# Revit family: SmartVide_120P_GENERADO
name_source: partatom
category: Equipos especializados
units: mm (PartAtom-declared; Revit-internal decimal feet)

## family parameters
Compartido = No
Corte con vacíos al cargar = No
Cota de conector redondo = Diámetro de uso
Número OmniClass = 23.21.21.13
Punto de cálculo de habitación = No
Se basa en plano de trabajo = No
Siempre vertical = Sí
Tipo de pieza = Normal

## types (8) — shared parameters
Fabricante = SAMMIC S.L.
Foodservice Equipment Identifier = Sí
Phase = 1
Revision Code = 1
URL = https://www.sammic.com
URL Cutsheet = http://www.sammic.com
zero-valued in all types: Elevación por defecto

## per-type parameters (varying)
| type | Comentarios de tipo | Conn Plug | Cycle | Depth | FL Amps | HP | Height | Modelo | Specification by Manufacturer | Volts | Watts | Weight in Pounds | Width |
| Heated tank 28P 28 l / 7.4 gal 230/50-60/1 | Tanks of 28 l / 7.4 gal and 56 l / 14.8 gal . | EU (SCHUKO 2P+G) | 50 Hz | 540 mm  [stored 1.77165 ft] | 3 A | 1.01 | 288 mm  [stored 0.944882 ft] | 1180070 | Connected to and controlled by SmartVide X to reach the set temperature faster. | 230 V | 750 W | 20.4 | 335 mm  [stored 1.09908 ft] |
| Heated tank 28P 28 l / 7.4 gal 120/60/1 | Tanks of 28 l / 7.4 gal and 56 l / 14.8 gal . | USA (NEMA 5-15P / 2P+G) | 60 Hz | 540 mm  [stored 1.77165 ft] | 6 A | 1.01 | 288 mm  [stored 0.944882 ft] | 1180071 | Connected to and controlled by SmartVide X to reach the set temperature faster. | 120 V | 750 W | 20.4 | 335 mm  [stored 1.09908 ft] |
| Heated tank 56P 56 l / 14.8 gal 230/50-60/1 | Tanks of 28 l / 7.4 gal and 56 l / 14.8 gal . | EU (SCHUKO 2P+G) | 50 Hz | 540 mm  [stored 1.77165 ft] | 6 A | 2.01 | 288 mm  [stored 0.944882 ft] | 1180075 | Connected to and controlled by SmartVide X to reach the set temperature faster. | 230 V | 1500 W | 36.8 | 660 mm  [stored 2.16535 ft] |
| Heated tank 56P 56 l / 14.8 gal 120/60/1 | Tanks of 28 l / 7.4 gal and 56 l / 14.8 gal . | USA (NEMA 5-15P / 2P+G) | 60 Hz | 540 mm  [stored 1.77165 ft] | 13 A | 2.01 | 288 mm  [stored 0.944882 ft] | 1180076 | Connected to and controlled by SmartVide X to reach the set temperature faster. | 120 V | 1500 W | 36.8 | 660 mm  [stored 2.16535 ft] |
| Heated tank 120 l / 30 gal SmartVide 120/60/1 | Connected to and controlled by SmartVide XL. | USA (NEMA 5-15P / 2P+G) | 60 Hz | 582 mm  [stored 1.90945 ft] | 13 A | 2.01 | 850 mm  [stored 2.78871 ft] | 1180421 | Connected to and controlled by SmartVide XL to reach the set temperature faster. | 120 V | 1500 W | 86 | 738 mm  [stored 2.42126 ft] |
| Heated tank 120P 120 l / 30 gal 208-240/50-60/1 | Connected to and controlled by SmartVide XL. | USA (NEMA 6-20P / 2P) | 50 Hz | 582 mm  [stored 1.90945 ft] | 6 A | 4.02 | 850 mm  [stored 2.78871 ft] | 1180422 | Connected to and controlled by SmartVide XL to reach the set temperature faster. | 208 V | 3000 W | 86 | 738 mm  [stored 2.42126 ft] |
| Heated tank 120 l / 30 gal SmartVide 230/50-60/1 | Connected to and controlled by SmartVide XL. | EU (SCHUKO 2P+G) | 50 Hz | 582 mm  [stored 1.90945 ft] | 6 A | 4.02 | 850 mm  [stored 2.78871 ft] | 1180420 | Connected to and controlled by SmartVide XL to reach the set temperature faster. | 230 V | 3000 W | 86 | 738 mm  [stored 2.42126 ft] |
| Heated tank 120P 230/5060/1 AUS | Connected to and controlled by SmartVide XL. | AUS | 50 Hz | 582 mm  [stored 1.90945 ft] | 6 A | 4.02 | 850 mm  [stored 2.78871 ft] | 1180424 | Connected to and controlled by SmartVide XL to reach the set temperature faster. | 230 V | 3000 W | 86 | 738 mm  [stored 2.42126 ft] |

note: column(s) folded — value = type name in every type: Descripción

note: [stored X ft] marks values corroborated as IEEE doubles in the binary element streams (Revit-internal decimal feet)
